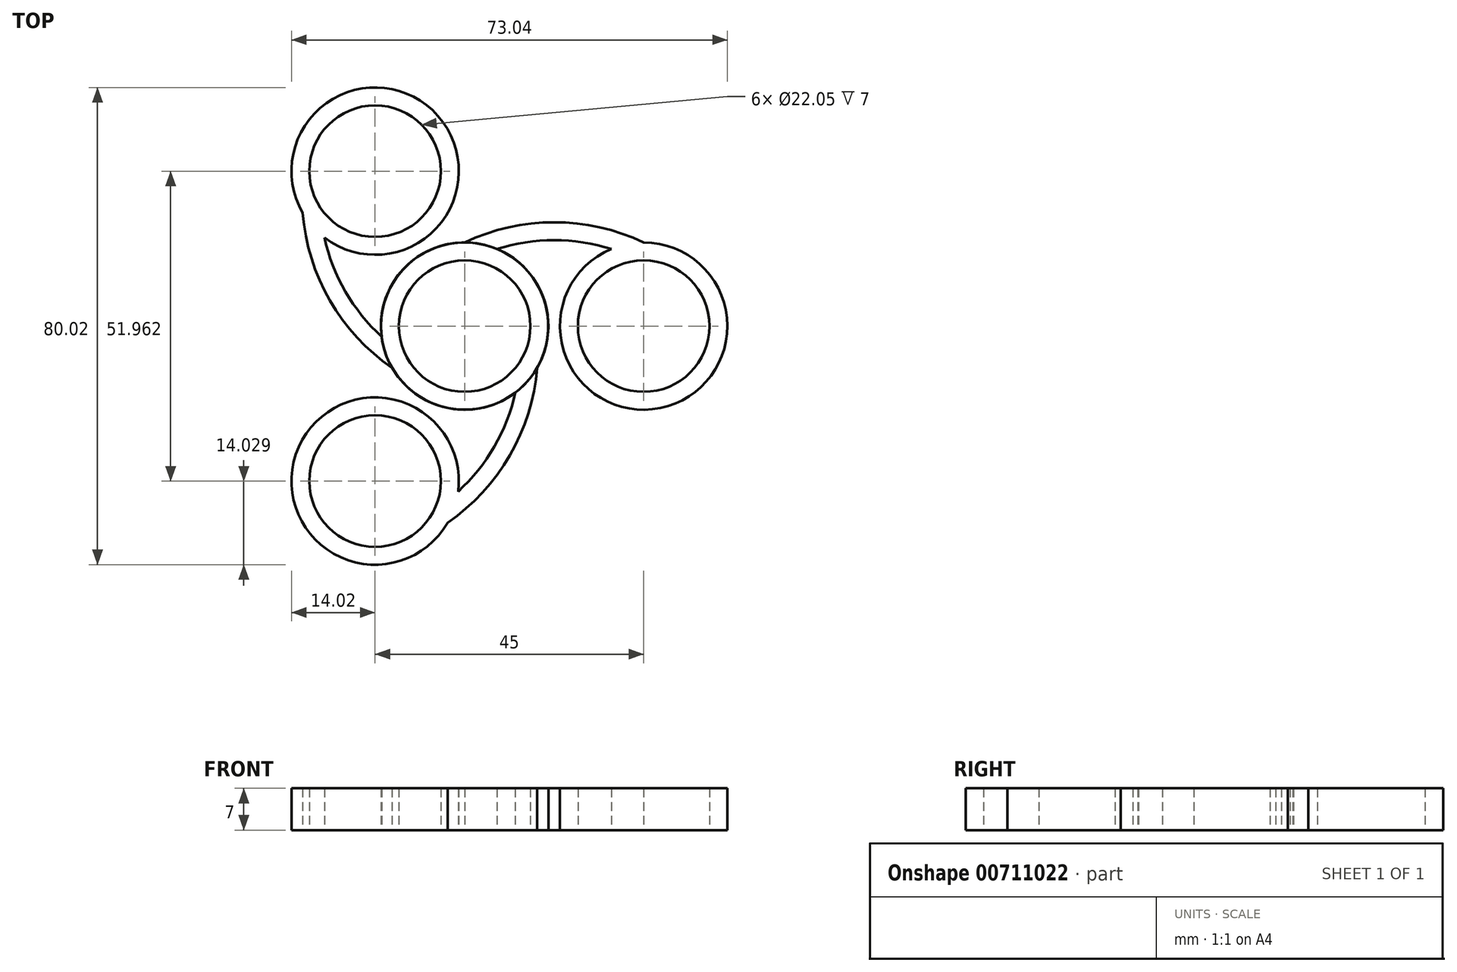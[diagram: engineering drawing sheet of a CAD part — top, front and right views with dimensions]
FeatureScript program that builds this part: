
annotation { "Feature Type Name" : "Feature", "Feature Type Description" : "" }
export const myFeature = defineFeature(function(context is Context, id is Id, definition is map)
    precondition{}
    {
        {
            var Q0;
            Q0=qCreatedBy(makeId("Top.planeOp"),FACE);
            var sketch = newSketch(context, id + "F0", { "sketchPlane" : qUnion([Q0])});
            skCircle(sketch, "E0", {"center": v(0, 0) * mm, "radius": 11.03 * mm});
            skCircle(sketch, "E1.0", {"center": v(0, 0) * mm, "radius": 14.02 * mm});
            skCircle(sketch, "E2.1.0.0", {"center": v(30, 0) * mm, "radius": 11.03 * mm});
            skCircle(sketch, "E2.1.0.1", {"center": v(30, 0) * mm, "radius": 14.02 * mm});
            skLineSegment(sketch, "E2.direction1", {"start": v(0, 0) * mm, "end": v(30, 0) * mm, "construction": true});
            skLineSegment(sketch, "E3", {"start": v(30, 25.13) * mm, "end": v(30, -41.78) * mm});
            skArc(sketch, "E4", {"start": v(30, 14.03) * mm, "mid": v(15, 17.4) * mm, "end": v(0, 14.02) * mm});
            skArc(sketch, "E5.0", {"start": v(28.71, 11.31) * mm, "mid": v(15, 14.4) * mm, "end": v(1.29, 11.31) * mm});
            skArc(sketch, "E6.MirrorCS", {"start": v(28.71, -11.31) * mm, "mid": v(15, -14.4) * mm, "end": v(1.29, -11.31) * mm});
            skArc(sketch, "E7.MirrorCS", {"start": v(30, -14.03) * mm, "mid": v(15, -17.4) * mm, "end": v(0, -14.02) * mm});
            skSolve(sketch);
        }
        {
            var Q0;
            {var subQ0=sQuery(id+"F0.wireOp",EDGE,"E3");var subQ1=sQuery(id+"F0.wireOp",EDGE,"E2.1.0.0");var subQ2=makeQuery(id+"F0.imprint","INTERSECT",VERTEX,{"disambiguationData":[OD(0.0)],"derivedFrom":[subQ1,subQ0]});Q0=makeQuery(id+"F0.imprint","IMPRINT",FACE,{"disambiguationData":[TD([[makeQuery(id+"F0.imprint","IMPRINT",EDGE,{"disambiguationData":[TD([[subQ2,1.0]])],"derivedFrom":subQ1}),-1.0]])]});}
            var Q1;
            {var subQ0=sQuery(id+"F0.wireOp",EDGE,"E3");var subQ6=sQuery(id+"F0.wireOp",EDGE,"E2.1.0.0");var subQ7=makeQuery(id+"F0.imprint","INTERSECT",VERTEX,{"disambiguationData":[OD(0.0)],"derivedFrom":[subQ6,subQ0]});Q1=makeQuery(id+"F0.imprint","IMPRINT",FACE,{"disambiguationData":[TD([[makeQuery(id+"F0.imprint","IMPRINT",EDGE,{"disambiguationData":[TD([[subQ7,-1.0]])],"derivedFrom":subQ6}),-1.0]])]});}
            var Q2;
            {var subQ0=sQuery(id+"F0.wireOp",EDGE,"E4");Q2=makeQuery(id+"F0.imprint","IMPRINT",FACE,{"disambiguationData":[TD([[makeQuery(id+"F0.imprint","IMPRINT",EDGE,{"derivedFrom":subQ0}),1.0]])]});}
            var Q3;
            {var subQ0=sQuery(id+"F0.wireOp",EDGE,"E7.MirrorCS");Q3=makeQuery(id+"F0.imprint","IMPRINT",FACE,{"disambiguationData":[TD([[makeQuery(id+"F0.imprint","IMPRINT",EDGE,{"derivedFrom":subQ0}),-1.0]])]});}
            var Q4;
            Q4=makeQuery(id+"F0.imprint","IMPRINT",FACE,{"disambiguationData":[TD([[makeQuery(id+"F0.imprint","IMPRINT",EDGE,{"derivedFrom":sQuery(id+"F0.wireOp",EDGE,"E0")}),-1.0]])]});
            extrude(context, id + "F1", {"entities" : qUnion([Q0, Q1, Q2, Q3, Q4]), "depth" : 7 * mm, "offsetDistance" : 25 * mm});
        }
        {
            var Q0;
            Q0=makeQuery(id+"F1.opExtrude","SWEPT_BODY",BODY,{"disambiguationData":[OSD([sQuery(id+"F0.wireOp",EDGE,"E0"),sQuery(id+"F0.wireOp",EDGE,"E1.0"),sQuery(id+"F0.wireOp",EDGE,"ddfe1a80-111f-40ba-aa11-5838728418130.MirrorC"),sQuery(id+"F0.wireOp",EDGE,"ddfe1a80-111f-40ba-aa11-5838728418131.MirrorC"),sQuery(id+"F0.wireOp",EDGE,"WN3oxOSN-cVLn-UZjw-D7Z1-LqRepIl2l9xi"),sQuery(id+"F0.wireOp",EDGE,"065204ab-c5dd-4cf8-a66f-a6cb3593be3f0.MirrorCS")])]});
            var Q1;
            Q1=makeQuery(id+"F1.opExtrude","CAP_EDGE",EDGE,{"disambiguationData":[OSD([sQuery(id+"F0.wireOp",EDGE,"E0")])],"isStart":false});
            circularPattern(context, id + "F2", {"entities" : qUnion([Q0]), "axis" : qUnion([Q1]), "angle" : 360 * degree, "instanceCount" : 3, "equalSpace" : true});
        }
    });
